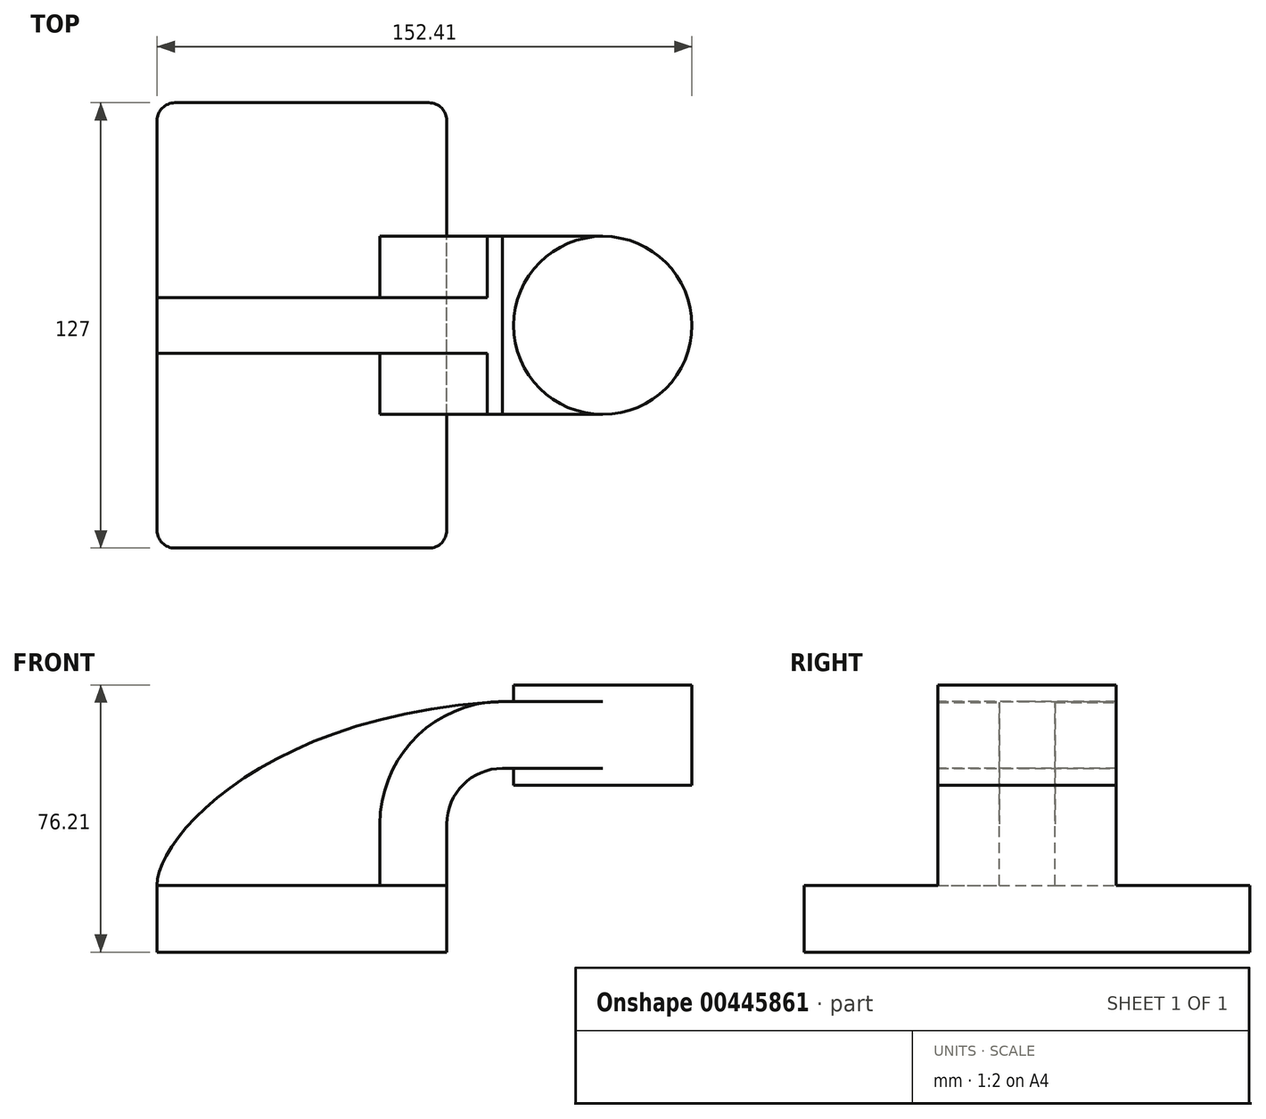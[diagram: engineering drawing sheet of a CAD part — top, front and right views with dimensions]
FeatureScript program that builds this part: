
annotation { "Feature Type Name" : "Feature", "Feature Type Description" : "" }
export const myFeature = defineFeature(function(context is Context, id is Id, definition is map)
    precondition{}
    {
        {
            var Q0;
            Q0=qCreatedBy(makeId("Front.planeOp"),FACE);
            var sketch = newSketch(context, id + "F0", { "sketchPlane" : qUnion([Q0])});
            skLineSegment(sketch, "E0.bottom", {"start": v(-41.28, -9.53) * mm, "end": v(41.28, -9.53) * mm});
            skLineSegment(sketch, "E0.top", {"start": v(-41.28, 9.53) * mm, "end": v(41.28, 9.53) * mm});
            skLineSegment(sketch, "E0.left", {"start": v(-41.28, -9.53) * mm, "end": v(-41.28, 9.53) * mm});
            skLineSegment(sketch, "E0.right", {"start": v(41.28, -9.53) * mm, "end": v(41.28, 9.53) * mm});
            skPoint(sketch, "E0.middle", {"position": v(0, 0) * mm});
            skLineSegment(sketch, "E1.bottom", {"start": v(111.12, 38.1) * mm, "end": v(60.32, 38.1) * mm});
            skLineSegment(sketch, "E1.top", {"start": v(111.13, 66.67) * mm, "end": v(60.33, 66.67) * mm});
            skLineSegment(sketch, "E1.left", {"start": v(111.12, 38.1) * mm, "end": v(111.12, 66.67) * mm});
            skLineSegment(sketch, "E1.right", {"start": v(60.32, 38.1) * mm, "end": v(60.32, 66.67) * mm});
            skPoint(sketch, "E1.middle", {"position": v(85.72, 52.39) * mm});
            skLineSegment(sketch, "E2", {"start": v(41.28, 9.52) * mm, "end": v(41.28, 27) * mm});
            skArc(sketch, "E3", {"start": v(41.28, 27) * mm, "mid": v(45.92, 38.23) * mm, "end": v(57.15, 42.88) * mm});
            skLineSegment(sketch, "E4", {"start": v(57.15, 42.88) * mm, "end": v(85.72, 42.88) * mm});
            skLineSegment(sketch, "E5.0", {"start": v(57.15, 61.93) * mm, "end": v(85.72, 61.93) * mm});
            skArc(sketch, "E5.1", {"start": v(22.23, 27) * mm, "mid": v(32.45, 51.7) * mm, "end": v(57.15, 61.93) * mm});
            skLineSegment(sketch, "E5.2", {"start": v(22.23, 9.52) * mm, "end": v(22.23, 27) * mm});
            skPoint(sketch, "E6", {"position": v(85.72, 38.1) * mm});
            skLineSegment(sketch, "E7", {"start": v(85.72, 38.1) * mm, "end": v(85.72, 66.67) * mm});
            skFitSpline(sketch, "E8", {"points": [v(-41.28, 9.53) * mm, v(57.15, 61.93) * mm], "startDerivative": vector(-0.83, 40.4) * mm, "endDerivative": vector(202.52, 10.45) * mm});
            skSolve(sketch);
        }
        {
            var Q0;
            Q0=makeQuery(id+"F0.imprint","IMPRINT",FACE,{"disambiguationData":[TD([[makeQuery(id+"F0.imprint","IMPRINT",EDGE,{"derivedFrom":sQuery(id+"F0.wireOp",EDGE,"E0.bottom")}),1.0]])]});
            extrude(context, id + "F1", {"entities" : qUnion([Q0]), "endBound" : BoundingType.SYMMETRIC, "depth" : 127 * mm});
        }
        {
            var Q0;
            {var subQ1=sQuery(id+"F0.wireOp",EDGE,"E2");Q0=makeQuery(id+"F0.imprint","IMPRINT",FACE,{"disambiguationData":[TD([[makeQuery(id+"F0.imprint","IMPRINT",EDGE,{"derivedFrom":subQ1}),1.0]])]});}
            var Q1;
            {var subQ0=sQuery(id+"F0.wireOp",EDGE,"E4");var subQ1=sQuery(id+"F0.wireOp",EDGE,"E1.right");var subQ2=makeQuery(id+"F0.imprint","INTERSECT",VERTEX,{"derivedFrom":[subQ1,subQ0]});Q1=makeQuery(id+"F0.imprint","IMPRINT",FACE,{"disambiguationData":[TD([[makeQuery(id+"F0.imprint","IMPRINT",EDGE,{"disambiguationData":[TD([[subQ2,-1.0]])],"derivedFrom":subQ1}),-1.0]])]});}
            extrude(context, id + "F2", {"entities" : qUnion([Q0, Q1]), "operationType" : NewBodyOperationType.ADD, "endBound" : BoundingType.SYMMETRIC, "depth" : 50.8 * mm});
        }
        {
            var Q0;
            {var subQ3=sQuery(id+"F0.wireOp",EDGE,"E5.2");Q0=makeQuery(id+"F0.imprint","IMPRINT",FACE,{"disambiguationData":[TD([[makeQuery(id+"F0.imprint","IMPRINT",EDGE,{"derivedFrom":subQ3}),1.0]])]});}
            extrude(context, id + "F3", {"entities" : qUnion([Q0]), "operationType" : NewBodyOperationType.ADD, "endBound" : BoundingType.SYMMETRIC, "depth" : 15.88 * mm});
        }
        {
            var Q0;
            {var subQ0=sQuery(id+"F0.wireOp",EDGE,"E1.left");Q0=makeQuery(id+"F0.imprint","IMPRINT",FACE,{"disambiguationData":[TD([[makeQuery(id+"F0.imprint","IMPRINT",EDGE,{"derivedFrom":subQ0}),1.0]])]});}
            var Q1;
            Q1=sQuery(id+"F0.wireOp",EDGE,"E7");
            revolve(context, id + "F4", {"operationType" : NewBodyOperationType.ADD, "entities" : qUnion([Q0]), "axis" : qUnion([Q1]), "revolveType" : RevolveType.FULL});
        }
        {
            var Q0;
            Q0=makeQuery(id+"F1.opExtrude","CAP_EDGE",EDGE,{"disambiguationData":[OSD([sQuery(id+"F0.wireOp",EDGE,"E0.right")])],"isStart":false});
            var Q1;
            Q1=makeQuery(id+"F1.opExtrude","CAP_EDGE",EDGE,{"disambiguationData":[OSD([sQuery(id+"F0.wireOp",EDGE,"E0.left")])],"isStart":false});
            var Q2;
            Q2=makeQuery(id+"F1.opExtrude","CAP_EDGE",EDGE,{"disambiguationData":[OSD([sQuery(id+"F0.wireOp",EDGE,"E0.right")])],"isStart":true});
            var Q3;
            Q3=makeQuery(id+"F1.opExtrude","CAP_EDGE",EDGE,{"disambiguationData":[OSD([sQuery(id+"F0.wireOp",EDGE,"E0.left")])],"isStart":true});
            fillet(context, id + "F5", {"entities" : qUnion([Q0, Q1, Q2, Q3]), "radius" : 5.08 * mm, "tangentPropagation" : true, "allowEdgeOverflow" : false});
        }
    });
